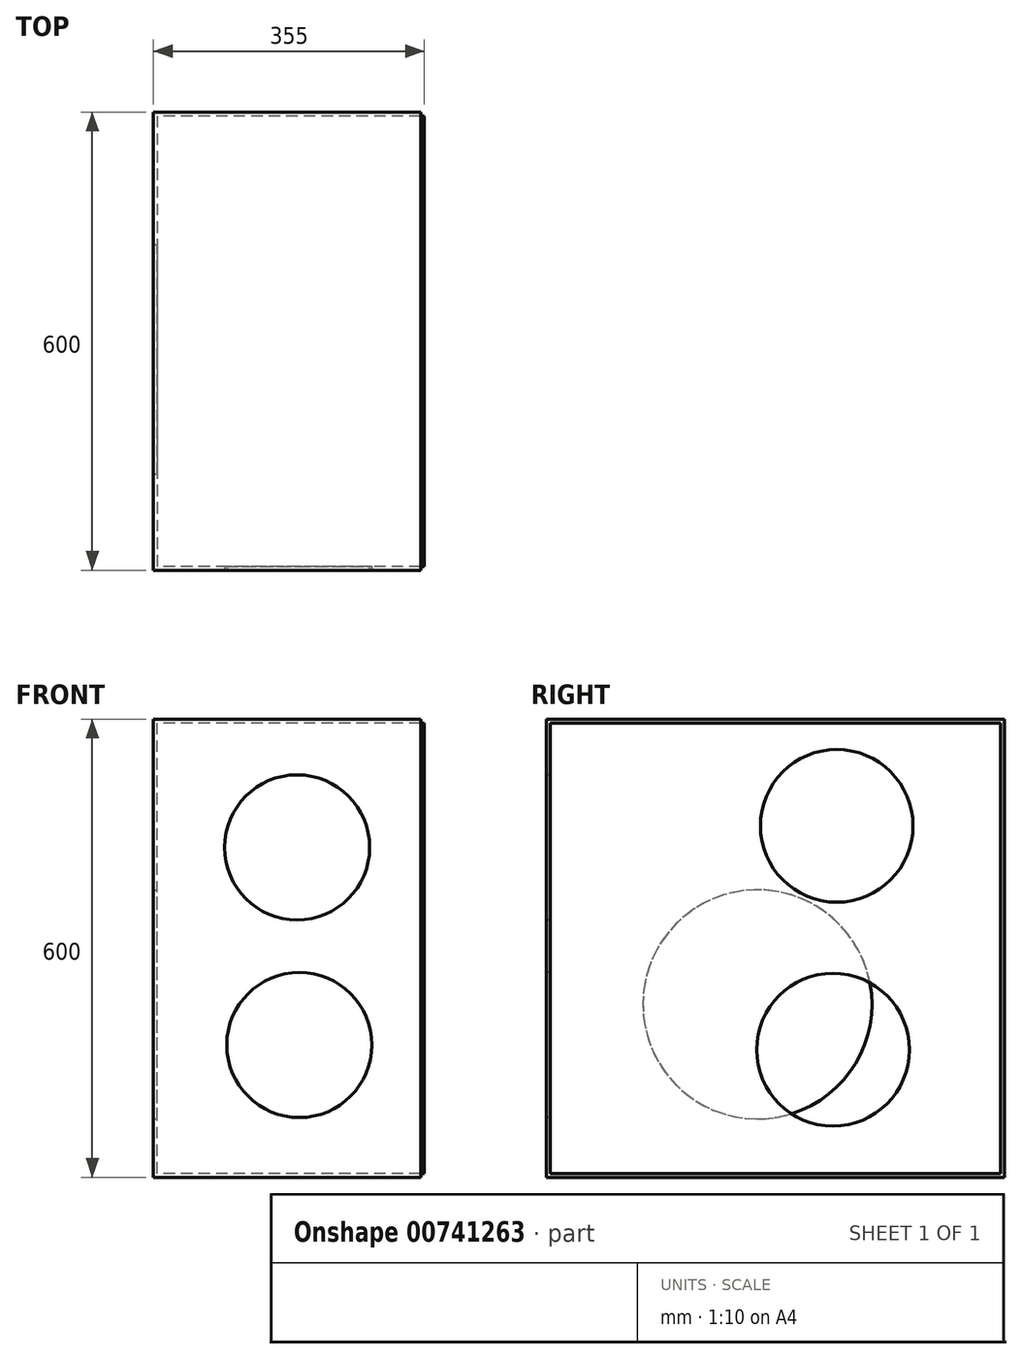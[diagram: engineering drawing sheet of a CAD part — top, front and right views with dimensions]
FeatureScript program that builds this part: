
annotation { "Feature Type Name" : "Feature", "Feature Type Description" : "" }
export const myFeature = defineFeature(function(context is Context, id is Id, definition is map)
    precondition{}
    {
        {
            var Q0;
            Q0=qCreatedBy(makeId("Right.planeOp"),FACE);
            var sketch = newSketch(context, id + "F0", { "sketchPlane" : qUnion([Q0])});
            skLineSegment(sketch, "E0.bottom", {"start": v(600, -600) * mm, "end": v(0, -600) * mm});
            skLineSegment(sketch, "E0.top", {"start": v(600, 0) * mm, "end": v(0, 0) * mm});
            skLineSegment(sketch, "E0.left", {"start": v(600, -600) * mm, "end": v(600, 0) * mm});
            skLineSegment(sketch, "E0.right", {"start": v(0, -600) * mm, "end": v(0, 0) * mm});
            skLineSegment(sketch, "E1.0", {"start": v(5, -595) * mm, "end": v(5, -5) * mm});
            skLineSegment(sketch, "E1.1", {"start": v(595, -595) * mm, "end": v(5, -595) * mm});
            skLineSegment(sketch, "E1.2", {"start": v(595, -595) * mm, "end": v(595, -5) * mm});
            skLineSegment(sketch, "E1.3", {"start": v(595, -5) * mm, "end": v(5, -5) * mm});
            skSolve(sketch);
        }
        {
            var Q0;
            Q0=makeQuery(id+"FyGdKy7c29rBfMh_0.imprint","IMPRINT",FACE,{"disambiguationData":[TD([[makeQuery(id+"FyGdKy7c29rBfMh_0.imprint","IMPRINT",EDGE,{"derivedFrom":makeQuery(id+"F0.imprint","IMPRINT",EDGE,{"derivedFrom":sQuery(id+"F0.wireOp",EDGE,"E1.0")})}),-1.0]])]});
            var Q1;
            Q1=makeQuery(id+"F0.imprint","IMPRINT",FACE,{"disambiguationData":[TD([[makeQuery(id+"F0.imprint","IMPRINT",EDGE,{"derivedFrom":sQuery(id+"F0.wireOp",EDGE,"E0.bottom")}),-1.0]])]});
            extrude(context, id + "F1", {"entities" : qUnion([Q0, Q1]), "depth" : 350 * mm, "offsetDistance" : 25 * mm});
        }
        {
            var Q0;
            Q0=makeQuery(id+"F0.imprint","IMPRINT",FACE,{"disambiguationData":[TD([[makeQuery(id+"F0.imprint","IMPRINT",EDGE,{"derivedFrom":sQuery(id+"F0.wireOp",EDGE,"E1.0")}),-1.0]])]});
            extrude(context, id + "F2", {"entities" : qUnion([Q0]), "operationType" : NewBodyOperationType.ADD, "depth" : 5 * mm, "offsetDistance" : 25 * mm});
        }
        {
            var Q0;
            Q0=makeQuery(id+"F2.opExtrude","CAP_FACE",FACE,{"disambiguationData":[OSD([sQuery(id+"F0.wireOp",EDGE,"E1.0"),sQuery(id+"F0.wireOp",EDGE,"E1.1"),sQuery(id+"F0.wireOp",EDGE,"E1.2"),sQuery(id+"F0.wireOp",EDGE,"E1.3")])],"isStart":false});
            var sketch = newSketch(context, id + "F3", { "sketchPlane" : qUnion([Q0])});
            skCircle(sketch, "E2", {"center": v(276.2, -373.58) * mm, "radius": 150 * mm});
            skSolve(sketch);
        }
        {
            var Q0;
            Q0=makeQuery(id+"F3.imprint","IMPRINT",FACE,{"disambiguationData":[TD([[makeQuery(id+"F3.imprint","IMPRINT",EDGE,{"derivedFrom":sQuery(id+"F3.wireOp",EDGE,"E2")}),1.0]])]});
            extrude(context, id + "F4", {"entities" : qUnion([Q0]), "operationType" : NewBodyOperationType.REMOVE, "oppositeDirection" : true, "depth" : 25 * mm, "offsetDistance" : 25 * mm});
        }
        {
            var Q0;
            Q0=makeQuery(id+"F1.opExtrude","SWEPT_FACE",FACE,{"disambiguationData":[OSD([sQuery(id+"F0.wireOp",EDGE,"E0.right")])]});
            var sketch = newSketch(context, id + "F5", { "sketchPlane" : qUnion([Q0])});
            skCircle(sketch, "E3", {"center": v(191.06, -426.7) * mm, "radius": 95 * mm});
            skCircle(sketch, "E4", {"center": v(188.11, -167.98) * mm, "radius": 95 * mm});
            skSolve(sketch);
        }
        {
            var Q0;
            Q0 = qSketchRegion(id + "F5", true);
            extrude(context, id + "F6", {"entities" : qUnion([Q0]), "operationType" : NewBodyOperationType.REMOVE, "oppositeDirection" : true, "depth" : 25 * mm, "offsetDistance" : 25 * mm});
        }
        {
            var Q0;
            Q0=makeQuery(id+"F1.opExtrude","CAP_FACE",FACE,{"disambiguationData":[OSD([sQuery(id+"F0.wireOp",EDGE,"E0.bottom"),sQuery(id+"F0.wireOp",EDGE,"E0.top"),sQuery(id+"F0.wireOp",EDGE,"E0.left"),sQuery(id+"F0.wireOp",EDGE,"E0.right"),sQuery(id+"F0.wireOp",EDGE,"E1.0"),sQuery(id+"F0.wireOp",EDGE,"E1.1"),sQuery(id+"F0.wireOp",EDGE,"E1.2"),sQuery(id+"F0.wireOp",EDGE,"E1.3")])],"isStart":false});
            var sketch = newSketch(context, id + "F7", { "sketchPlane" : qUnion([Q0])});
            skLineSegment(sketch, "E5.bottom", {"start": v(5, -5) * mm, "end": v(595, -5) * mm});
            skLineSegment(sketch, "E5.top", {"start": v(5, -595) * mm, "end": v(595, -595) * mm});
            skLineSegment(sketch, "E5.left", {"start": v(5, -5) * mm, "end": v(5, -595) * mm});
            skLineSegment(sketch, "E5.right", {"start": v(595, -5) * mm, "end": v(595, -595) * mm});
            skSolve(sketch);
        }
        {
            var Q0;
            Q0 = qSketchRegion(id + "F7", true);
            extrude(context, id + "F8", {"entities" : qUnion([Q0]), "depth" : 5 * mm, "offsetDistance" : 25 * mm});
        }
        {
            var Q0;
            Q0=makeQuery(id+"F1.opExtrude","SWEPT_FACE",FACE,{"disambiguationData":[OSD([sQuery(id+"F0.wireOp",EDGE,"E0.right")])]});
            var sketch = newSketch(context, id + "F9", { "sketchPlane" : qUnion([Q0])});
            skCircle(sketch, "E6.0", {"center": v(191.06, -426.7) * mm, "radius": 100 * mm});
            skSolve(sketch);
        }
        {
            var Q0;
            Q0=makeQuery(id+"F9.imprint","IMPRINT",FACE,{"disambiguationData":[TD([[makeQuery(id+"F9.imprint","IMPRINT",EDGE,{"derivedFrom":sQuery(id+"F9.wireOp",EDGE,"E6.0")}),-1.0]])]});
            var sketch = newSketch(context, id + "F10", { "sketchPlane" : qUnion([Q0])});
            skCircle(sketch, "E7.0", {"center": v(188.11, -167.98) * mm, "radius": 100 * mm});
            skSolve(sketch);
        }
        {
            var Q0;
            Q0=sQuery(id+"F9.wireOp",EDGE,"E6.0");
            var Q1;
            Q1=sQuery(id+"F10.wireOp",EDGE,"E7.0");
            extrude(context, id + "F11", {"bodyType" : ToolBodyType.SURFACE, "surfaceEntities" : qUnion([Q0, Q1]), "depth" : 35 * mm, "offsetDistance" : 25 * mm});
        }
        {
            var Q0;
            Q0=makeQuery(id+"F8.opExtrude","CAP_FACE",FACE,{"disambiguationData":[OSD([sQuery(id+"F7.wireOp",EDGE,"E5.bottom"),sQuery(id+"F7.wireOp",EDGE,"E5.top"),sQuery(id+"F7.wireOp",EDGE,"E5.left"),sQuery(id+"F7.wireOp",EDGE,"E5.right")])],"isStart":false});
            var sketch = newSketch(context, id + "F12", { "sketchPlane" : qUnion([Q0])});
            skCircle(sketch, "E8", {"center": v(380.07, -139.78) * mm, "radius": 100 * mm});
            skCircle(sketch, "E9", {"center": v(375.16, -432.95) * mm, "radius": 100 * mm});
            skSolve(sketch);
        }
        {
            var Q0;
            Q0=makeQuery(id+"F12.imprint","IMPRINT",FACE,{"disambiguationData":[TD([[makeQuery(id+"F12.imprint","IMPRINT",EDGE,{"derivedFrom":sQuery(id+"F12.wireOp",EDGE,"E8")}),1.0]])]});
            var Q1;
            Q1=makeQuery(id+"F12.imprint","IMPRINT",FACE,{"disambiguationData":[TD([[makeQuery(id+"F12.imprint","IMPRINT",EDGE,{"derivedFrom":sQuery(id+"F12.wireOp",EDGE,"E9")}),1.0]])]});
            extrude(context, id + "F13", {"entities" : qUnion([Q0, Q1]), "operationType" : NewBodyOperationType.REMOVE, "oppositeDirection" : true, "depth" : 25 * mm, "offsetDistance" : 25 * mm});
        }
    });
